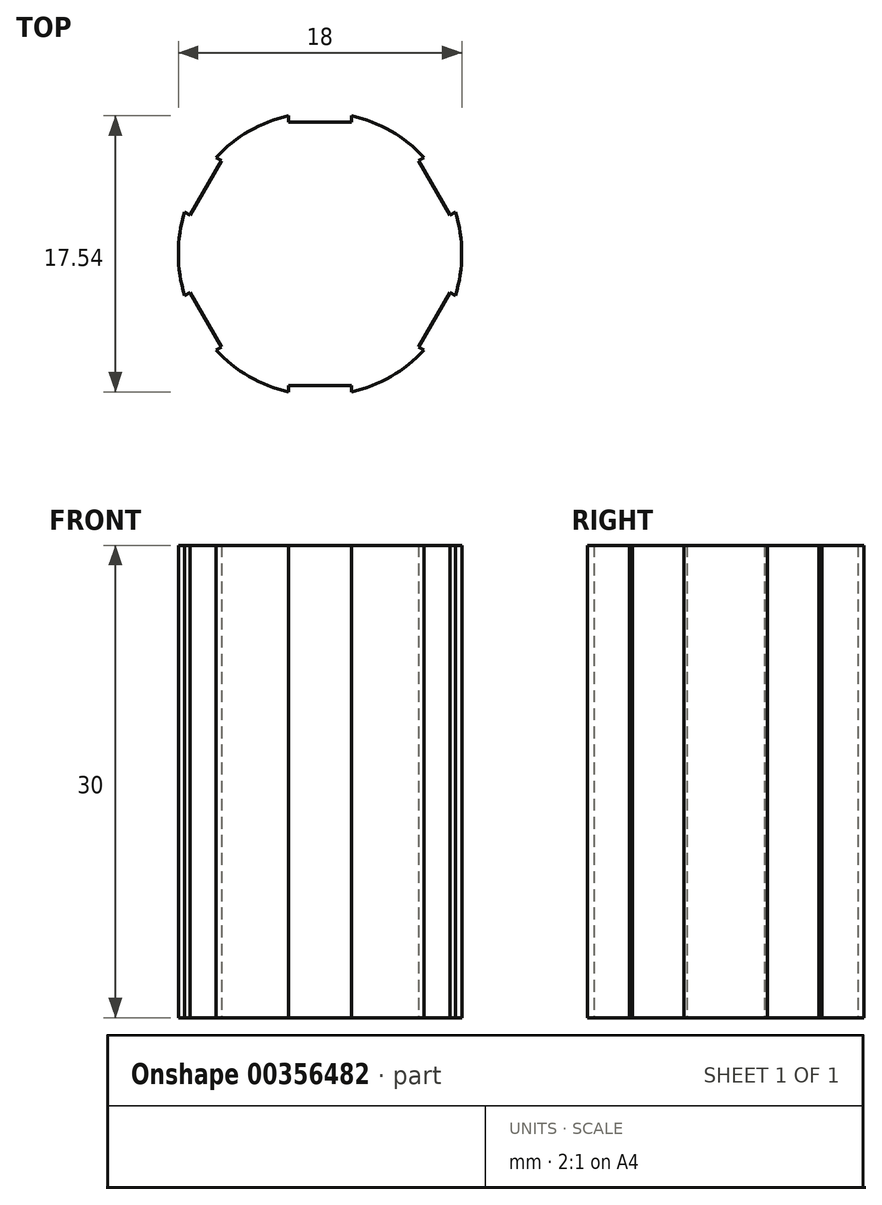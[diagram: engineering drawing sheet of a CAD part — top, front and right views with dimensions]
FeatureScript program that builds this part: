
annotation { "Feature Type Name" : "Feature", "Feature Type Description" : "" }
export const myFeature = defineFeature(function(context is Context, id is Id, definition is map)
    precondition{}
    {
        {
            var Q0;
            Q0=qCreatedBy(makeId("Top.planeOp"),FACE);
            var sketch = newSketch(context, id + "F0", { "sketchPlane" : qUnion([Q0])});
            skCircle(sketch, "E0", {"center": v(0, 0) * mm, "radius": 10 * mm});
            skArc(sketch, "E1", {"start": v(2, -8.77) * mm, "mid": v(4.5, -7.8) * mm, "end": v(6.6, -6.12) * mm});
            skLineSegment(sketch, "E2.left", {"start": v(2, 8.77) * mm, "end": v(2, 8.38) * mm});
            skLineSegment(sketch, "E2.right", {"start": v(-2, 8.77) * mm, "end": v(-2, 8.38) * mm});
            skLineSegment(sketch, "E3.MirrorCS", {"start": v(-8.6, -2.66) * mm, "end": v(-8.26, -2.46) * mm});
            skLineSegment(sketch, "E4.MirrorCS", {"start": v(-6.6, -6.12) * mm, "end": v(-6.26, -5.92) * mm});
            skLineSegment(sketch, "E5.MirrorCS", {"start": v(-6.6, 6.12) * mm, "end": v(-6.26, 5.92) * mm});
            skLineSegment(sketch, "E6.MirrorCS", {"start": v(-8.6, 2.66) * mm, "end": v(-8.26, 2.46) * mm});
            skPoint(sketch, "E7.orphan", {"position": v(-8.72, 7.35) * mm});
            skPoint(sketch, "E8.orphan", {"position": v(-10.72, 3.88) * mm});
            skPoint(sketch, "E9.orphan", {"position": v(-10.72, -3.88) * mm});
            skPoint(sketch, "E10.orphan", {"position": v(-8.72, -7.35) * mm});
            skPoint(sketch, "E2.top.end.orphan", {"position": v(-2, -11.23) * mm});
            skPoint(sketch, "E11.orphan", {"position": v(2, -11.23) * mm});
            skPoint(sketch, "E12.orphan", {"position": v(8.72, -7.35) * mm});
            skPoint(sketch, "E13.orphan", {"position": v(10.72, -3.88) * mm});
            skPoint(sketch, "E14.orphan", {"position": v(10.72, 3.88) * mm});
            skPoint(sketch, "E15.orphan", {"position": v(8.72, 7.35) * mm});
            skPoint(sketch, "E16.orphan", {"position": v(2, 11.23) * mm});
            skPoint(sketch, "E17.orphan", {"position": v(-2, 11.23) * mm});
            skLineSegment(sketch, "E18", {"start": v(-8.26, -2.46) * mm, "end": v(-6.26, -5.92) * mm});
            skLineSegment(sketch, "E19.MirrorCS", {"start": v(8.26, -2.46) * mm, "end": v(6.26, -5.92) * mm});
            skLineSegment(sketch, "E20.MirrorCS", {"start": v(-8.26, 2.46) * mm, "end": v(-6.26, 5.92) * mm});
            skLineSegment(sketch, "E21.MirrorCS", {"start": v(8.26, 2.46) * mm, "end": v(6.26, 5.92) * mm});
            skLineSegment(sketch, "E22.MirrorCS", {"start": v(2, 8.38) * mm, "end": v(-2, 8.38) * mm});
            skLineSegment(sketch, "E23.MirrorCS", {"start": v(-2, -8.38) * mm, "end": v(2, -8.38) * mm});
            skLineSegment(sketch, "E24.trimOffspring", {"start": v(6.26, 5.92) * mm, "end": v(6.6, 6.12) * mm});
            skLineSegment(sketch, "E25.trimOffspring", {"start": v(8.26, 2.46) * mm, "end": v(8.6, 2.66) * mm});
            skLineSegment(sketch, "E26.trimOffspring", {"start": v(8.26, -2.46) * mm, "end": v(8.6, -2.66) * mm});
            skLineSegment(sketch, "E27.trimOffspring", {"start": v(6.26, -5.92) * mm, "end": v(6.6, -6.12) * mm});
            skLineSegment(sketch, "E28.trimOffspring", {"start": v(2, -8.38) * mm, "end": v(2, -8.77) * mm});
            skLineSegment(sketch, "E29.trimOffspring", {"start": v(-2, -8.38) * mm, "end": v(-2, -8.77) * mm});
            skArc(sketch, "E30.trimOffspring", {"start": v(-6.6, -6.12) * mm, "mid": v(-4.5, -7.8) * mm, "end": v(-2, -8.77) * mm});
            skArc(sketch, "E31.trimOffspring", {"start": v(-8.6, 2.66) * mm, "mid": v(-9, 0) * mm, "end": v(-8.6, -2.66) * mm});
            skArc(sketch, "E32.trimOffspring", {"start": v(-2, 8.77) * mm, "mid": v(-4.5, 7.8) * mm, "end": v(-6.6, 6.12) * mm});
            skArc(sketch, "E33.trimOffspring", {"start": v(6.6, 6.12) * mm, "mid": v(4.5, 7.8) * mm, "end": v(2, 8.77) * mm});
            skArc(sketch, "E34.trimOffspring", {"start": v(8.6, -2.66) * mm, "mid": v(9, 0) * mm, "end": v(8.6, 2.66) * mm});
            skSolve(sketch);
        }
        {
            var Q0;
            Q0=makeQuery(id+"F0.imprint","IMPRINT",FACE,{"disambiguationData":[TD([[makeQuery(id+"F0.imprint","IMPRINT",EDGE,{"derivedFrom":sQuery(id+"F0.wireOp",EDGE,"E1")}),1.0]])]});
            extrude(context, id + "F1", {"entities" : qUnion([Q0]), "depth" : 30 * mm});
        }
    });
